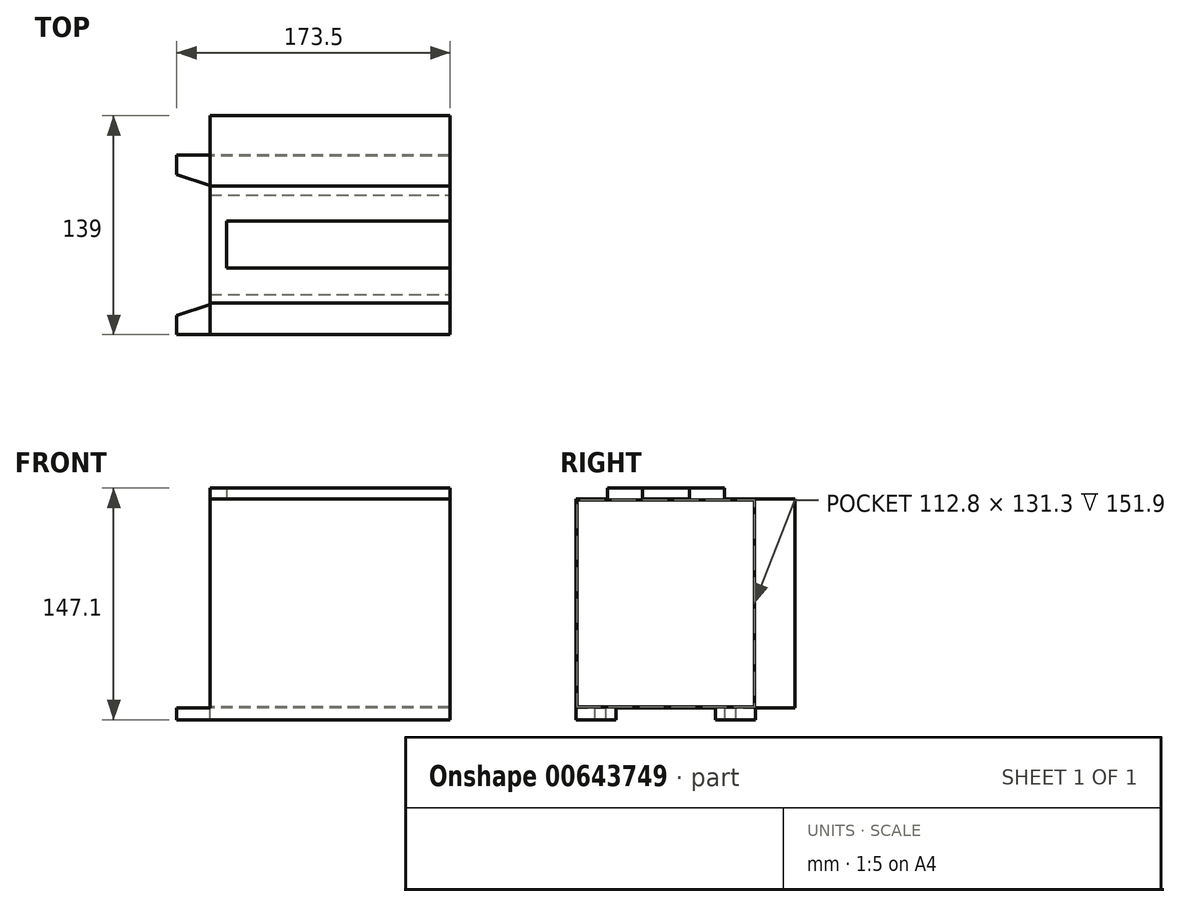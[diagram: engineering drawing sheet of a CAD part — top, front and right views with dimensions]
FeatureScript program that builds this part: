
annotation { "Feature Type Name" : "Feature", "Feature Type Description" : "" }
export const myFeature = defineFeature(function(context is Context, id is Id, definition is map)
    precondition{}
    {
        {
            var Q0;
            Q0=qCreatedBy(makeId("Top.planeOp"),FACE);
            var sketch = newSketch(context, id + "F0", { "sketchPlane" : qUnion([Q0])});
            skLineSegment(sketch, "E0.bottom", {"start": v(0, 0) * mm, "end": v(152.5, 0) * mm});
            skLineSegment(sketch, "E0.top", {"start": v(0, 114) * mm, "end": v(152.5, 114) * mm});
            skLineSegment(sketch, "E0.left", {"start": v(0, 0) * mm, "end": v(0, 114) * mm});
            skLineSegment(sketch, "E0.right", {"start": v(152.5, 0) * mm, "end": v(152.5, 114) * mm});
            skSolve(sketch);
        }
        {
            var Q0;
            Q0=qCreatedBy(makeId("Front.planeOp"),FACE);
            var sketch = newSketch(context, id + "F1", { "sketchPlane" : qUnion([Q0])});
            skLineSegment(sketch, "E1.bottom", {"start": v(0, 0) * mm, "end": v(152.5, 0) * mm});
            skLineSegment(sketch, "E1.top", {"start": v(0, 132.5) * mm, "end": v(152.5, 132.5) * mm});
            skLineSegment(sketch, "E1.left", {"start": v(0, 0) * mm, "end": v(0, 132.5) * mm});
            skLineSegment(sketch, "E1.right", {"start": v(152.5, 0) * mm, "end": v(152.5, 132.5) * mm});
            skSolve(sketch);
        }
        {
            var Q0;
            Q0=sQuery(id+"F0.wireOp",EDGE,"E0.left");
            var Q1;
            Q1=sQuery(id+"F0.wireOp",VERTEX,"E0.left.end");
            cPlane(context, id + "F2", {"entities" : qUnion([Q0, Q1]), "cplaneType" : CPlaneType.LINE_POINT, "offset" : 25 * mm, "width" : 150 * mm, "height" : 150 * mm});
        }
        {
            var Q0;
            Q0=qCreatedBy(id+"F2.planeOp",FACE);
            var sketch = newSketch(context, id + "F3", { "sketchPlane" : qUnion([Q0])});
            skLineSegment(sketch, "E2.bottom", {"start": v(-152.5, 0) * mm, "end": v(0, 0) * mm});
            skLineSegment(sketch, "E2.top", {"start": v(-152.5, 132.5) * mm, "end": v(0, 132.5) * mm});
            skLineSegment(sketch, "E2.left", {"start": v(-152.5, 0) * mm, "end": v(-152.5, 132.5) * mm});
            skLineSegment(sketch, "E2.right", {"start": v(0, 0) * mm, "end": v(0, 132.5) * mm});
            skSolve(sketch);
        }
        {
            var Q0;
            Q0=sQuery(id+"F3.wireOp",EDGE,"E2.right");
            var Q1;
            Q1=sQuery(id+"F1.wireOp",VERTEX,"E1.left.end");
            cPlane(context, id + "F4", {"entities" : qUnion([Q0, Q1]), "cplaneType" : CPlaneType.LINE_POINT, "offset" : 25 * mm, "width" : 150 * mm, "height" : 150 * mm});
        }
        {
            var Q0;
            Q0=qCreatedBy(id+"F4.planeOp",FACE);
            var sketch = newSketch(context, id + "F5", { "sketchPlane" : qUnion([Q0])});
            skLineSegment(sketch, "E3.bottom", {"start": v(0, 0) * mm, "end": v(152.5, 0) * mm});
            skLineSegment(sketch, "E3.top", {"start": v(0, 114) * mm, "end": v(152.5, 114) * mm});
            skLineSegment(sketch, "E3.left", {"start": v(0, 0) * mm, "end": v(0, 114) * mm});
            skLineSegment(sketch, "E3.right", {"start": v(152.5, 0) * mm, "end": v(152.5, 114) * mm});
            skSolve(sketch);
        }
        {
            var Q0;
            Q0=qCreatedBy(makeId("Right.planeOp"),FACE);
            var sketch = newSketch(context, id + "F6", { "sketchPlane" : qUnion([Q0])});
            skPoint(sketch, "E4.0", {"position": v(114, 132.5) * mm});
            skLineSegment(sketch, "E5.bottom", {"start": v(0, 0) * mm, "end": v(114, 0) * mm});
            skLineSegment(sketch, "E5.top", {"start": v(0, 132.5) * mm, "end": v(114, 132.5) * mm});
            skLineSegment(sketch, "E5.left", {"start": v(0, 0) * mm, "end": v(0, 132.5) * mm});
            skLineSegment(sketch, "E5.right", {"start": v(114, 0) * mm, "end": v(114, 132.5) * mm});
            skSolve(sketch);
        }
        {
            var Q0;
            Q0=makeQuery(id+"F6.imprint","IMPRINT",FACE,{"disambiguationData":[TD([[makeQuery(id+"F6.imprint","IMPRINT",EDGE,{"derivedFrom":sQuery(id+"F6.wireOp",EDGE,"E5.bottom")}),1.0]])]});
            extrude(context, id + "F7", {"entities" : qUnion([Q0]), "depth" : 0.6 * mm, "offsetDistance" : 25 * mm});
        }
        {
            assignVariable(context, id + "F8", {"name" : "x", "anyValue" : 0.6});
        }
        {
            var Q0;
            Q0=makeQuery(id+"F5.imprint","IMPRINT",FACE,{"disambiguationData":[TD([[makeQuery(id+"F5.imprint","IMPRINT",EDGE,{"derivedFrom":sQuery(id+"F5.wireOp",EDGE,"E3.bottom")}),1.0]])]});
            extrude(context, id + "F9", {"entities" : qUnion([Q0]), "operationType" : NewBodyOperationType.ADD, "oppositeDirection" : true, "depth" : (getVariable(context, 'x')) * mm, "offsetDistance" : 25 * mm});
        }
        {
            var Q0;
            Q0=makeQuery(id+"F1.imprint","IMPRINT",FACE,{"disambiguationData":[TD([[makeQuery(id+"F1.imprint","IMPRINT",EDGE,{"derivedFrom":sQuery(id+"F1.wireOp",EDGE,"E1.bottom")}),1.0]])]});
            extrude(context, id + "F10", {"entities" : qUnion([Q0]), "operationType" : NewBodyOperationType.ADD, "oppositeDirection" : true, "depth" : (getVariable(context, 'x')) * mm, "offsetDistance" : 25 * mm});
        }
        {
            var Q0;
            Q0=makeQuery(id+"F3.imprint","IMPRINT",FACE,{"disambiguationData":[TD([[makeQuery(id+"F3.imprint","IMPRINT",EDGE,{"derivedFrom":sQuery(id+"F3.wireOp",EDGE,"E2.bottom")}),1.0]])]});
            extrude(context, id + "F11", {"entities" : qUnion([Q0]), "operationType" : NewBodyOperationType.ADD, "oppositeDirection" : true, "depth" : (getVariable(context, 'x')) * mm, "offsetDistance" : 25 * mm});
        }
        {
            var Q0;
            Q0=makeQuery(id+"F0.imprint","IMPRINT",FACE,{"disambiguationData":[TD([[makeQuery(id+"F0.imprint","IMPRINT",EDGE,{"derivedFrom":sQuery(id+"F0.wireOp",EDGE,"E0.bottom")}),1.0]])]});
            extrude(context, id + "F12", {"entities" : qUnion([Q0]), "operationType" : NewBodyOperationType.ADD, "depth" : (getVariable(context, 'x')) * mm, "offsetDistance" : 25 * mm});
        }
        {
            var Q0;
            Q0=makeQuery(id+"F11.boolean.opBoolean","MERGE",FACE,{"derivedFrom":[makeQuery(id+"F9.boolean.opBoolean","MERGE",FACE,{"derivedFrom":[makeQuery(id+"F7.opExtrude","SWEPT_FACE",FACE,{"disambiguationData":[OSD([sQuery(id+"F6.wireOp",EDGE,"E5.right")])]}),makeQuery(id+"F9.opExtrude","SWEPT_FACE",FACE,{"disambiguationData":[OSD([sQuery(id+"F5.wireOp",EDGE,"E3.top")])]})]}),makeQuery(id+"F11.opExtrude","CAP_FACE",FACE,{"disambiguationData":[OSD([sQuery(id+"F3.wireOp",EDGE,"E2.bottom"),sQuery(id+"F3.wireOp",EDGE,"E2.top"),sQuery(id+"F3.wireOp",EDGE,"E2.left"),sQuery(id+"F3.wireOp",EDGE,"E2.right")])],"isStart":true})]});
            var sketch = newSketch(context, id + "F13", { "sketchPlane" : qUnion([Q0])});
            skLineSegment(sketch, "E6.bottom", {"start": v(-152.5, 132.5) * mm, "end": v(0, 132.5) * mm});
            skLineSegment(sketch, "E6.top", {"start": v(-152.5, 0) * mm, "end": v(0, 0) * mm});
            skLineSegment(sketch, "E6.left", {"start": v(-152.5, 132.5) * mm, "end": v(-152.5, 0) * mm});
            skLineSegment(sketch, "E6.right", {"start": v(0, 132.5) * mm, "end": v(0, 0) * mm});
            skSolve(sketch);
        }
        {
            var Q0;
            Q0 = qSketchRegion(id + "F13", true);
            extrude(context, id + "F14", {"entities" : qUnion([Q0]), "operationType" : NewBodyOperationType.ADD, "depth" : 25 * mm, "offsetDistance" : 25 * mm});
        }
        {
            var Q0;
            Q0=makeQuery(id+"F14.boolean.opBoolean","MERGE",FACE,{"derivedFrom":[makeQuery(id+"F9.boolean.opBoolean","MERGE",FACE,{"derivedFrom":[makeQuery(id+"F7.opExtrude","SWEPT_FACE",FACE,{"disambiguationData":[OSD([sQuery(id+"F6.wireOp",EDGE,"E5.top")])]}),makeQuery(id+"F9.opExtrude","CAP_FACE",FACE,{"disambiguationData":[OSD([sQuery(id+"F5.wireOp",EDGE,"E3.bottom"),sQuery(id+"F5.wireOp",EDGE,"E3.top"),sQuery(id+"F5.wireOp",EDGE,"E3.left"),sQuery(id+"F5.wireOp",EDGE,"E3.right")])],"isStart":true})]}),makeQuery(id+"F14.opExtrude","SWEPT_FACE",FACE,{"disambiguationData":[OSD([sQuery(id+"F13.wireOp",EDGE,"E6.bottom")])]})]});
            var sketch = newSketch(context, id + "F15", { "sketchPlane" : qUnion([Q0])});
            skLineSegment(sketch, "E7", {"start": v(0, 20) * mm, "end": v(152.5, 20) * mm});
            skLineSegment(sketch, "E8", {"start": v(152.5, 20) * mm, "end": v(152.5, 42.25) * mm});
            skLineSegment(sketch, "E9", {"start": v(152.5, 42.25) * mm, "end": v(10.78, 42.25) * mm});
            skLineSegment(sketch, "E10", {"start": v(10.78, 42.25) * mm, "end": v(10.78, 72.25) * mm});
            skLineSegment(sketch, "E11", {"start": v(10.78, 72.25) * mm, "end": v(152.5, 72.25) * mm});
            skLineSegment(sketch, "E12", {"start": v(152.5, 72.25) * mm, "end": v(152.5, 94.5) * mm});
            skLineSegment(sketch, "E13", {"start": v(152.5, 94.5) * mm, "end": v(0, 94.5) * mm});
            skLineSegment(sketch, "E14", {"start": v(0, 94.5) * mm, "end": v(0, 20) * mm});
            skSolve(sketch);
        }
        {
            var Q0;
            Q0 = qSketchRegion(id + "F15", true);
            extrude(context, id + "F16", {"entities" : qUnion([Q0]), "operationType" : NewBodyOperationType.ADD, "depth" : 7 * mm, "offsetDistance" : 25 * mm});
        }
        {
            var Q0;
            Q0=makeQuery(id+"F14.boolean.opBoolean","MERGE",FACE,{"derivedFrom":[makeQuery(id+"F12.boolean.opBoolean","MERGE",FACE,{"derivedFrom":[makeQuery(id+"F11.boolean.opBoolean","MERGE",FACE,{"derivedFrom":[makeQuery(id+"F10.boolean.opBoolean","MERGE",FACE,{"derivedFrom":[makeQuery(id+"F7.opExtrude","SWEPT_FACE",FACE,{"disambiguationData":[OSD([sQuery(id+"F6.wireOp",EDGE,"E5.bottom")])]}),makeQuery(id+"F10.opExtrude","SWEPT_FACE",FACE,{"disambiguationData":[OSD([sQuery(id+"F1.wireOp",EDGE,"E1.bottom")])]})]}),makeQuery(id+"F11.opExtrude","SWEPT_FACE",FACE,{"disambiguationData":[OSD([sQuery(id+"F3.wireOp",EDGE,"E2.bottom")])]})]}),makeQuery(id+"F12.opExtrude","CAP_FACE",FACE,{"disambiguationData":[OSD([sQuery(id+"F0.wireOp",EDGE,"E0.bottom"),sQuery(id+"F0.wireOp",EDGE,"E0.top"),sQuery(id+"F0.wireOp",EDGE,"E0.left"),sQuery(id+"F0.wireOp",EDGE,"E0.right")])],"isStart":true})]}),makeQuery(id+"F14.opExtrude","SWEPT_FACE",FACE,{"disambiguationData":[OSD([sQuery(id+"F13.wireOp",EDGE,"E6.top")])]})]});
            var sketch = newSketch(context, id + "F17", { "sketchPlane" : qUnion([Q0])});
            skLineSegment(sketch, "E15", {"start": v(152.5, 0) * mm, "end": v(0, 0) * mm});
            skLineSegment(sketch, "E16", {"start": v(0, 0) * mm, "end": v(-21, 0) * mm});
            skLineSegment(sketch, "E17", {"start": v(-21, 0) * mm, "end": v(-21, -12.25) * mm});
            skLineSegment(sketch, "E18", {"start": v(-21, -12.25) * mm, "end": v(0, -19.2) * mm});
            skLineSegment(sketch, "E19", {"start": v(0, -19.2) * mm, "end": v(0, -25.5) * mm});
            skLineSegment(sketch, "E20", {"start": v(0, -25.5) * mm, "end": v(152.5, -25.5) * mm});
            skLineSegment(sketch, "E21", {"start": v(152.5, -25.5) * mm, "end": v(152.5, 0) * mm});
            skLineSegment(sketch, "E22", {"start": v(152.5, -114) * mm, "end": v(0, -114) * mm});
            skLineSegment(sketch, "E23", {"start": v(0, -114) * mm, "end": v(-21, -114) * mm});
            skLineSegment(sketch, "E24", {"start": v(-21, -114) * mm, "end": v(-21, -101.75) * mm});
            skLineSegment(sketch, "E25", {"start": v(-21, -101.75) * mm, "end": v(0, -94.8) * mm});
            skLineSegment(sketch, "E26", {"start": v(0, -94.8) * mm, "end": v(0, -88.5) * mm});
            skLineSegment(sketch, "E27", {"start": v(0, -88.5) * mm, "end": v(152.5, -88.5) * mm});
            skLineSegment(sketch, "E28", {"start": v(152.5, -88.5) * mm, "end": v(152.5, -114) * mm});
            skSolve(sketch);
        }
        {
            var Q0;
            Q0 = qSketchRegion(id + "F17", true);
            extrude(context, id + "F18", {"entities" : qUnion([Q0]), "operationType" : NewBodyOperationType.ADD, "depth" : 7.6 * mm, "offsetDistance" : 25 * mm});
        }
    });
